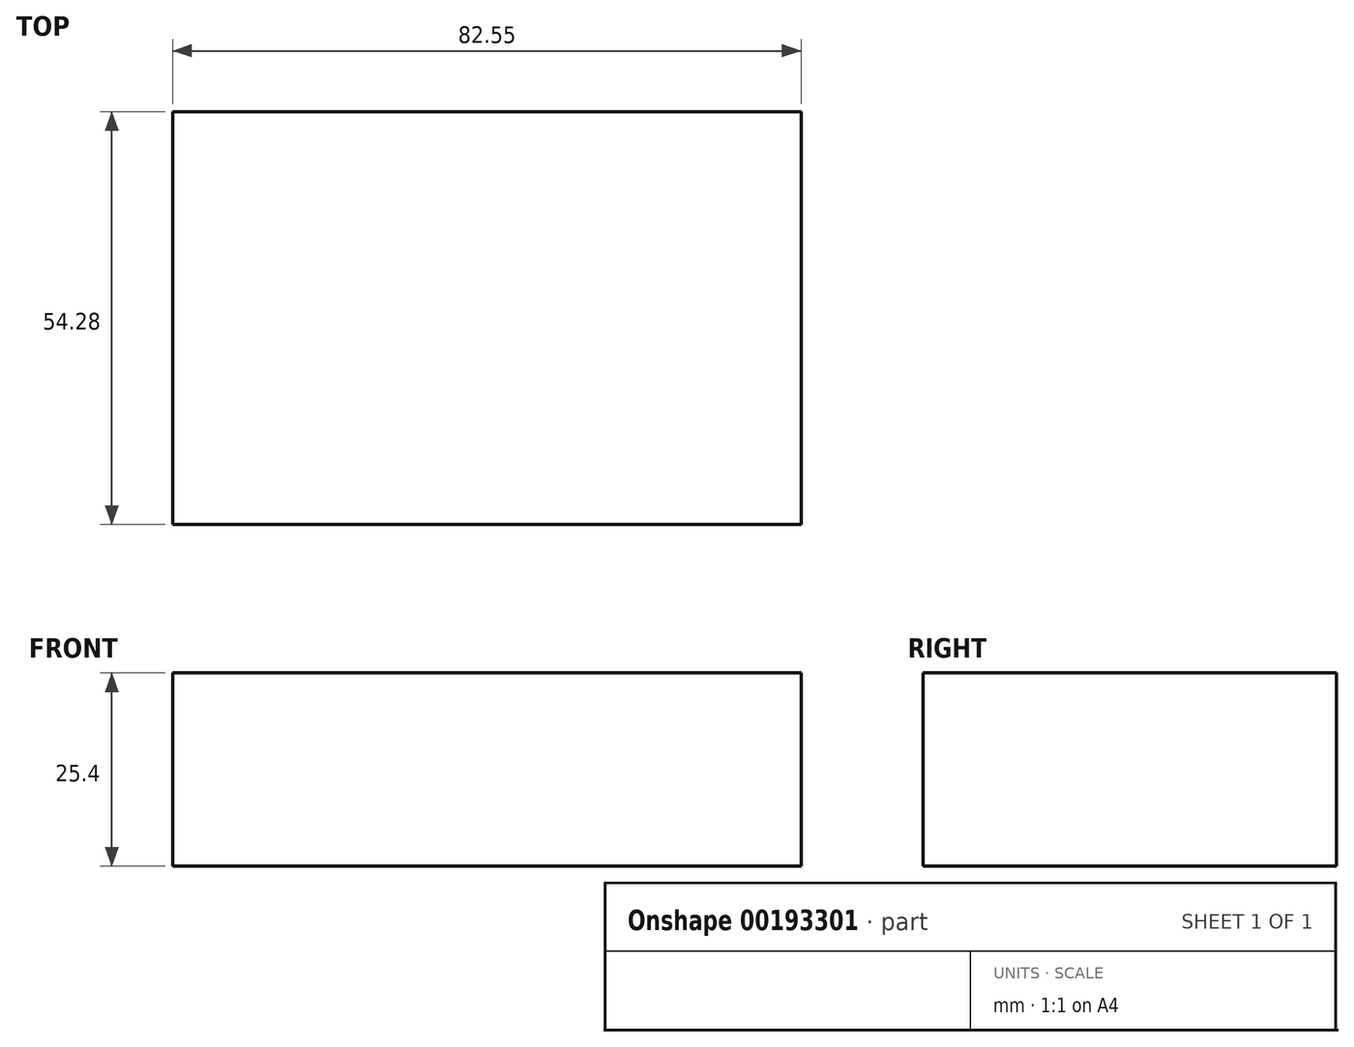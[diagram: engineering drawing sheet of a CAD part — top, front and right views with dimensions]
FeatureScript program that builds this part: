
annotation { "Feature Type Name" : "Feature", "Feature Type Description" : "" }
export const myFeature = defineFeature(function(context is Context, id is Id, definition is map)
    precondition{}
    {
        {
            var Q0;
            Q0=qCreatedBy(makeId("Top.planeOp"),FACE);
            var sketch = newSketch(context, id + "F0", { "sketchPlane" : qUnion([Q0])});
            skLineSegment(sketch, "E0.bottom", {"start": v(-31.85, 24.97) * mm, "end": v(50.7, 24.97) * mm});
            skLineSegment(sketch, "E0.top", {"start": v(-31.85, -29.3) * mm, "end": v(50.7, -29.3) * mm});
            skLineSegment(sketch, "E0.left", {"start": v(-31.85, 24.97) * mm, "end": v(-31.85, -29.3) * mm});
            skLineSegment(sketch, "E0.right", {"start": v(50.7, 24.97) * mm, "end": v(50.7, -29.3) * mm});
            skSolve(sketch);
        }
        {
            var Q0;
            Q0 = qSketchRegion(id + "F0", true);
            extrude(context, id + "F1", {"entities" : qUnion([Q0]), "depth" : 25.4 * mm});
        }
        {
            var Q0;
            Q0=makeQuery(id+"F1.opExtrude","CAP_FACE",FACE,{"disambiguationData":[OSD([sQuery(id+"F0.wireOp",EDGE,"E0.bottom"),sQuery(id+"F0.wireOp",EDGE,"E0.top"),sQuery(id+"F0.wireOp",EDGE,"E0.left"),sQuery(id+"F0.wireOp",EDGE,"E0.right")])],"isStart":false});
            var sketch = newSketch(context, id + "F2", { "sketchPlane" : qUnion([Q0])});
            skCircle(sketch, "E1", {"center": v(-18.28, 14.6) * mm, "radius": 23.4 * mm});
            skLineSegment(sketch, "E2", {"start": v(7.16, 42.5) * mm, "end": v(21.68, -20.26) * mm});
            skSolve(sketch);
        }
        {
            var Q0;
            Q0=sQuery(id+"F2.wireOp",EDGE,"E1");
            var Q1;
            Q1=sQuery(id+"F2.wireOp",EDGE,"E2");
            revolve(context, id + "F3", {"bodyType" : ToolBodyType.SURFACE, "surfaceEntities" : qUnion([Q0]), "axis" : qUnion([Q1]), "revolveType" : RevolveType.FULL});
        }
    });
